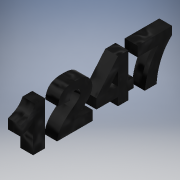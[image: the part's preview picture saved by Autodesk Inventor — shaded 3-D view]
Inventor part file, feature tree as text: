
AUTODESK INVENTOR PART (.ipt)
format: ipt  version: 2017 (Build 210142000, 142)  size: 814,592 bytes
history: native  units: in
note: dims shown in document units (in); Inventor stores cm internally (conversion verified against a paired STEP export)
features: sketch x24, extrude x18, projected_geometry x11, plane x9, loft x4, other x3, mirror x1, emboss x1, fillet x1
ambient origin geometry x8: Origin, YZ Plane, XZ Plane, XY Plane, X Axis, Y Axis, Z Axis, Center Point
bodies: Solid1 (feature_tree)
feature tree (72):
  sketch  "Sketch1"  dims[d0=0.7559in d1=0.7559in]
  plane  "Work Plane1"
  loft  "Loft1"
  extrude  "Extrusion1"  Depth=0.2in
  plane  "Work Plane4"
  loft  "Loft2"
  plane  "Work Plane5"
  loft  "Loft3"
  loft  "Loft4"
  extrude  "Extrusion2"  TaperAngle=0.0deg  [1 undecoded]
  plane  "Work Plane6"
  extrude  "Extrusion3"  Depth=1.0in
  extrude  "Extrusion4"  Depth=1.0651in
  extrude  "Extrusion5"  Depth=0.962in
  plane  "Work Plane7"
  extrude  "Extrusion6"  Depth=0.075in
  plane  "Work Plane8"
  other  "Work Axis1"
  plane  "Work Plane9"
  extrude  "Extrusion7"  Depth=0.06in
  mirror  "Mirror3"
  extrude  "Extrusion8"  Depth=0.05in
  plane  "Work Plane10"
  extrude  "Extrusion9"  Depth=0.0625in
  plane  "Work Plane11"
  extrude  "Extrusion10"  Depth=0.075in
  extrude  "Extrusion11"  TaperAngle=0.0deg  [1 undecoded]
  extrude  "Extrusion12"  Depth=0.2in
  extrude  "Extrusion13"  TaperAngle=0.0deg  [1 undecoded]
  emboss  "Emboss1"
  extrude  "Extrusion16"  Depth=0.01in
  extrude  "Extrusion17"  Depth=0.0344in
  extrude  "Extrusion18"  TaperAngle=60.0deg  [1 undecoded]
  fillet  "Fillet1"  [1 undecoded]
  extrude  "Extrusion19"  Depth=0.05in
  extrude  "Extrusion20"  Depth=0.05in
  sketch  "Sketch2"  dims[d2=0.9963in d3=0.2in]
  sketch  "Sketch3"  dims[d4=0.5in d6=0.08in]
  sketch  "Sketch4"  dims[d7=0.55in d8=150.0deg]
  other  "Edges1"
  sketch  "Sketch5"  dims[d9=150.0deg d14=0.33in]
  projected_geometry  "Projected Loop1"
  other  "Edges2"
  sketch  "Sketch6"  dims[d15=0.66in d18=0.0in d19=90.0deg]
  sketch  "Sketch7"  dims[d20=0.0in d21=90.0deg d22=1.0in]
  sketch  "Sketch8"  dims[d26=1.0651in d28=1.0651in]
  sketch  "Sketch9"  dims[d29=0.0in d30=0.962in]
  sketch  "Sketch10"  dims[d31=0.962in d32=0.075in]
  sketch  "Sketch11"  dims[d33=0.15in d34=0.06in]
  sketch  "Sketch12"  dims[d35=0.1in d36=0.05in]
  sketch  "Sketch13"  dims[d37=0.45in d38=0.0in d39=0.0625in]
  projected_geometry  "Projected Loop2"
  projected_geometry  "Projected Loop3"
  sketch  "Sketch14"  dims[d40=0.01in d41=0.075in]
  projected_geometry  "Projected Loop4"
  sketch  "Sketch15"  dims[d42=0.01in d43=0.0in d44=90.0deg]
  sketch  "Sketch16"  dims[d45=0.0in d46=90.0deg d47=0.2in]
  sketch  "Sketch17"  dims[d48=0.07in d49=0.0in d50=90.0deg]
  sketch  "Sketch18"  dims[d51=0.0in d52=90.0deg d53=0.01in]
  sketch  "Sketch19"  dims[d54=0.01in d55=0.0344in]
  sketch  "Sketch23"  dims[d56=150.0deg d57=60.0deg d58=150.0deg]
  projected_geometry  "Projected Loop6"
  sketch  "Sketch24"  dims[d59=0.7in d60=0.05in]
  sketch  "Sketch25"  dims[d61=0.05in d62=0.05in d63=0.05in]
  sketch  "Sketch26"  dims[d64=0.05in]
  projected_geometry  "Projected Loop7"
  projected_geometry  "Projected Loop8"
  sketch  "Sketch27"  dims[d65=0.01in d66=0.0in d67=90.0deg d68=0.0in d69=90.0deg d70=0.1in d71=0.4in d72=0.15in d73=0.05in d74=0.0in d75=0.02in d77=0.15in d78=0.02in d79=0.1in d80=0.1in d81=0.1in d82=0.02in d83=0.15in d84=0.05in d85=0.0in d86=0.045in d87=0.0in d88=0.025in d89=0.0in d90=0.02in d91=0.02in d92=0.005in d93=0.0in d94=90.0deg d95=0.4466in d96=1.0in d97=0.0in d98=1.0in d99=0.0in d100=0.6528in d101=0.0in d102=0.0in d103=1.0in d104=0.0in d106=90.0deg d107=1.0in d108=0.0in d109=1.65in d110=0.1in d111=0.1in d112=0.0in d113=0.1in d114=0.075in d115=0.0in d116=0.05in d117=0.0in d123=0.84in d124=0.8in d125=0.0in d126=0.0in d127=1.0in d128=0.0in d130=0.15in d131=-0.0206in d135=0.2in d136=0.05in d137=0.1in d138=0.05in d139=0.0in d140=0.025in d141=0.0in]
  projected_geometry  "Projected Loop9"
  projected_geometry  "Projected Loop10"
  projected_geometry  "Projected Loop11"
  projected_geometry  "Projected Loop12"
note: 5 required parameter values undecoded (feature->parameter linkage not recoverable at this tier; creation-order binding heuristic only, values carry confidence <= 0.55)
